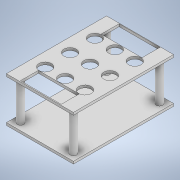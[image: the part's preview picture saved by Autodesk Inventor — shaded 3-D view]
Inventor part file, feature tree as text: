
AUTODESK INVENTOR PART (.ipt)
format: ipt  version: 2020 (Build 240168000, 168)  size: 204,800 bytes
history: native  units: in
note: dims shown in document units (in); Inventor stores cm internally (conversion verified against a paired STEP export)
features: extrude x4, sketch x3
ambient origin geometry x8: Origin, YZ Plane, XZ Plane, XY Plane, X Axis, Y Axis, Z Axis, Center Point
bodies: Solid1 (feature_tree)
feature tree (7):
  extrude  "Extrusion1"  Depth=5.0299in
  extrude  "Extrusion2"  Depth=0.125in
  extrude  "Extrusion3"  TaperAngle=45.0deg  [1 undecoded]
  extrude  "Extrusion4"  Depth=0.9in
  sketch  "Sketch1"  dims[d0=3.3654in d1=5.0299in]
  sketch  "Sketch2"  dims[d2=0.125in d3=0.0in d4=0.5in]
  sketch  "Sketch3"  dims[d5=0.5in d6=45.0deg d7=0.5in d8=45.0deg d9=0.5in d10=0.325in d11=0.325in d12=0.325in d13=0.325in d14=2.0in d15=0.0in d16=0.125in d17=0.0in d18=1.25in d19=90.0deg d20=1.25in d21=0.62in d22=0.62in d23=0.125in d24=0.0in d25=0.62in d26=1.0in d27=0.62in d28=1.0in d29=1.0in d30=1.0in d31=1.0in d32=1.0in d33=180.0deg d34=0.62in d35=0.62in d36=0.62in d37=0.62in d38=0.62in d39=2.05in d40=0.9in d41=2.05in d42=0.9in]
note: 1 required parameter value undecoded (feature->parameter linkage not recoverable at this tier; creation-order binding heuristic only, values carry confidence <= 0.55)
